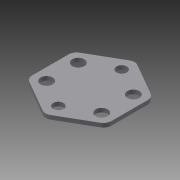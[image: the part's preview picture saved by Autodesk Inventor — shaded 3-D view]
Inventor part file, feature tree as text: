
AUTODESK INVENTOR PART (.ipt)
format: ipt  version: 2014 SP1 (Build 180222100, 222)  size: 112,640 bytes
history: native  units: in
note: dims shown in document units (in); Inventor stores cm internally (conversion verified against a paired STEP export)
features: extrude x1, sketch x1
ambient origin geometry x8: Origin, YZ Plane, XZ Plane, XY Plane, X Axis, Y Axis, Z Axis, Center Point
bodies: Solid1 (feature_tree)
feature tree (2):
  extrude  "Extrusion1"  Depth=0.0625in
  sketch  "Sketch1"  dims[d0=0.164in d1=0.164in d2=1.0in d3=0.19in d4=0.19in d5=0.5in d6=0.435in d7=0.435in d8=0.25in d9=0.19in d10=0.19in d11=0.435in d12=0.5in d13=1.25in d14=0.125in d15=0.0625in d16=0.0in]
